# Revit family: Plumbing-Showerheads-Sloan-Valve-AC-460z
name_source: partatom
category: Plumbing Fixtures
units: mm (PartAtom-declared; Revit-internal decimal feet)

## family parameters
Cut with Voids When Loaded = No
Host = Face
OmniClass Number = 23.45.05.14.99
OmniClass Title = Other Sanitary Washing Plumbing Fixtures
Part Type = Normal
Room Calculation Point = No
Round Connector Dimension = Use Diameter
Shared = No

## types (3) — shared parameters
Assembly Code = D2020300
CW Connection = Yes
Default Elevation = 0"
Description = Polished Chrome Finish, Act-O-Matic® Institutional Behind the WallInstallation Showerhead.
Diameter = 4 3/8"
Edition number = 1
HW Connection = No
Keynote = 15410
Manufacturer = Sloan Valve
Product Material = Sloan Valve - Finish - Polished Chrome
URL = www.sloanvalve.com
Valve Pressure Drop = 0.00 psi
Vent Connection = No
Waste Connection = No
Water Inlet Connection Description = Water Inlet Connection
Water Inlet Connection Diameter = 1"
zero-valued in all types: CWFU, HWFU, WFU

## per-type parameters (varying)
| type | Part Number | Water Flow |
| AC-460-1.8GPM-CP | 4024631 | 2 GPM |
| AC-460-2.0GPM-CP | 4024630 | 2 GPM |
| AC-460-2.5GPM-CP | 4024600 | 3 GPM |

note: column(s) folded — value = type name in every type: Model

## geometry (parser evidence)
native form markers: Sweep x2
no freeform markers — native parametric forms only
